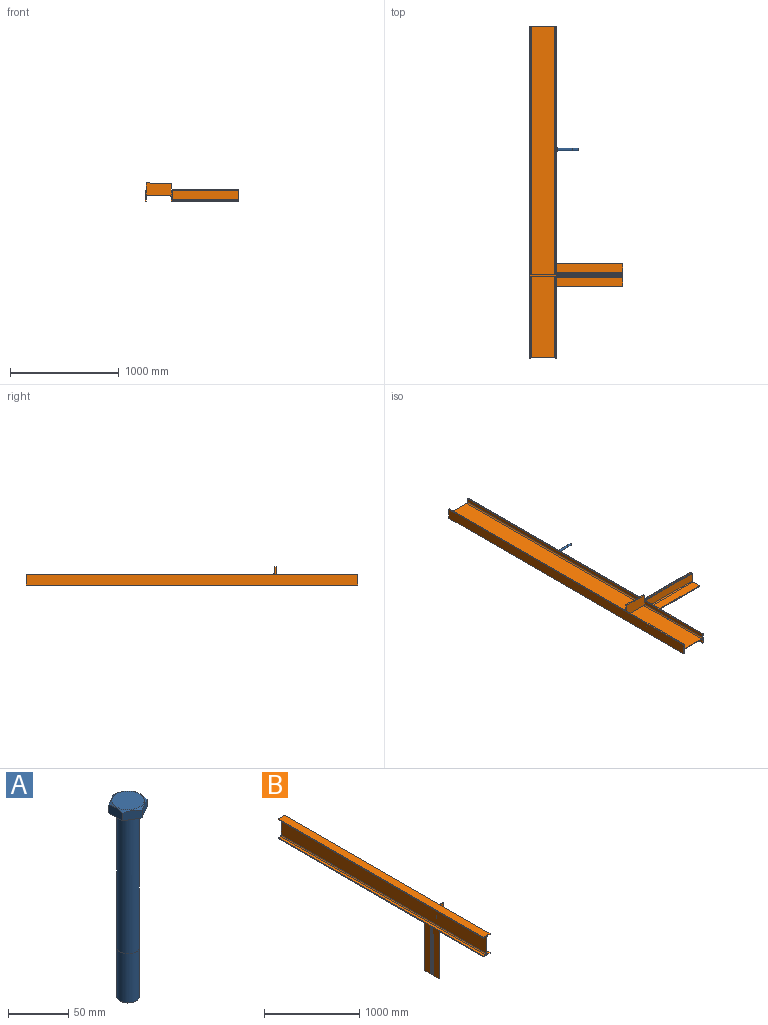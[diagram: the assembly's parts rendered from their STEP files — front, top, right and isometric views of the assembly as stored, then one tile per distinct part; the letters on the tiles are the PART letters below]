
ASSEMBLY  parts=2 mates=1
PART A: 17 faces, bbox 33x33x200.4 mm
  f0: cylinder r=9.53mm len=138.94mm, axis (0,0,-1), area 8315.1mm2, adj f1,f7
  f1: torus R=10.29mm, axis (0,0,1), area 73.7mm2, adj f0,f6
  f2: cylinder r=13.49mm len=26.99mm, axis (0,0,-1), area 32.3mm2, adj f6,f8
  f3: cone r=13.49mm half-angle=60deg, axis (0,0,-1), area 156mm2, adj f9,f10,f11,f12,f13,f14,f15
  f4: cylinder r=9.42mm len=50.04mm, axis (0,0,-1), area 2960.7mm2, adj f5,f7
  f5: cone r=8.66mm half-angle=45deg, axis (0,0,1), area 61.2mm2, adj f4,f16
  f6: plane 26.99x26.99mm, normal (0,0,-1), area 239.6mm2, adj f1,f2
  f7: plane 19.05x19.05mm, normal (0,0,-1), area 6.4mm2, adj f0,f4
  f8: plane 33x28.58mm, normal (0,0,-1), area 135.1mm2, adj f2,f10,f11,f12,f13,f14,f15
  f9: plane 26.99x26.99mm, normal (0,0,1), area 572mm2, adj f3
  f10: plane 16.5x9.08mm, normal (1,0,0), area 142.6mm2, adj f3,f8,f11,f15
  f11: plane 14.29x9.08mm, normal (0.5,-0.87,0), area 142.5mm2, adj f3,f8,f10,f12
  f12: plane 14.29x9.08mm, normal (-0.5,-0.87,0), area 142.6mm2, adj f3,f8,f11,f13
  f13: plane 16.5x9.08mm, normal (-1,0,0), area 142.6mm2, adj f3,f8,f12,f14
  f14: plane 14.29x9.08mm, normal (-0.5,0.87,0), area 142.6mm2, adj f3,f8,f13,f15
  f15: plane 14.29x9.08mm, normal (0.5,0.87,0), area 142.6mm2, adj f3,f8,f10,f14
  f16: plane 17.31x17.31mm, normal (0,0,-1), area 235.3mm2, adj f5
PART B: 50 faces, bbox 166.2x3048x860.3 mm
  f0: plane 2286x36mm, normal (0,0,1), area 82306.3mm2, adj f13,f15,f24,f49
  f1: plane 2286x212.6mm, normal (1,0,0), area 485999mm2, adj f15,f17,f24,f49
  f2: plane 2286x36mm, normal (0,0,-1), area 82306.3mm2, adj f17,f19,f24,f49
  f3: cylinder r=12.16mm len=749.3mm, axis (0,1,0), area 12323.9mm2, adj f14,f16,f23,f48
  f4: cylinder r=12.16mm len=749.3mm, axis (0,1,0), area 12323.9mm2, adj f16,f18,f23,f48
  f5: plane 100.58x12.7mm, normal (0,0,-1), area 1277.4mm2, adj f11,f13,f33,f43
  f6: plane 2274.15x100.58mm, normal (0,0,-1), area 228036mm2, adj f11,f13,f24,f37,f38,f39,f40,f41
  f7: cylinder r=12.16mm len=3048mm, axis (0,1,0), area 50131mm2, adj f8,f22,f23,f24
  f8: plane 3048x212.6mm, normal (-1,0,0), area 647998.7mm2, adj f7,f9,f23,f24
  f9: cylinder r=12.16mm len=3048mm, axis (0,1,0), area 50131mm2, adj f8,f10,f23,f24
  f10: plane 3048x36mm, normal (0,0,1), area 109741.7mm2, adj f9,f11,f23,f24
  f11: plane 3048x619.13mm, normal (-1,0,0), area 152902.9mm2, adj f5,f6,f10,f12,f23,f24,f26,f32
  f12: plane 750.15x100.58mm, normal (0,0,-1), area 74746mm2, adj f11,f13,f23,f27,f28,f29,f30,f31
  f13: plane 3048x9.53mm, normal (1,0,0), area 29032.2mm2, adj f0,f5,f6,f12,f14,f23,f24,f25
  f14: plane 749.3x36mm, normal (0,0,1), area 26978.2mm2, adj f3,f13,f23,f48
  f15: cylinder r=12.16mm len=2286mm, axis (0,1,0), area 37598.2mm2, adj f0,f1,f24,f49
  f16: plane 749.3x212.6mm, normal (1,0,0), area 159299.7mm2, adj f3,f4,f23,f48
  f17: cylinder r=12.16mm len=2286mm, axis (0,1,0), area 37598.2mm2, adj f1,f2,f24,f49
  f18: plane 749.3x36mm, normal (0,0,-1), area 26978.2mm2, adj f4,f19,f23,f48
  f19: plane 3048x9.53mm, normal (1,0,0), area 29032.2mm2, adj f2,f18,f20,f23,f24,f45
  f20: plane 3048x100.58mm, normal (0,0,1), area 306580mm2, adj f19,f21,f23,f24
  f21: plane 3048x9.53mm, normal (-1,0,0), area 29032.2mm2, adj f20,f22,f23,f24
  f22: plane 3048x36mm, normal (0,0,-1), area 109741.7mm2, adj f7,f21,f23,f24
  f23: plane 250.7x100.58mm, normal (0,-1,0), area 3149mm2, adj f3,f4,f7,f8,f9,f10,f11,f12
  f24: plane 250.7x100.58mm, normal (0,1,0), area 3149mm2, adj f0,f1,f2,f6,f7,f8,f9,f10
  f25: plane 5.5x1.02mm, normal (0,0,1), area 4.9mm2, adj f13,f27,f33,f34
  f26: plane 101.6x101.6mm, normal (0,0,-1), area 1265.1mm2, adj f11,f27,f28,f29,f30,f31,f32,f33
  f27: cylinder r=3.17mm len=609.6mm, axis (0,0,-1), area 3040.3mm2, adj f12,f25,f26,f28,f34
  f28: plane 609.6x82.55mm, normal (0,-1,0), area 50322.5mm2, adj f12,f26,f27,f29
  f29: cylinder r=9.52mm len=609.6mm, axis (0,0,-1), area 9120.8mm2, adj f12,f26,f28,f30
  f30: plane 609.6x82.55mm, normal (1,0,0), area 50322.5mm2, adj f12,f26,f29,f31
  f31: cylinder r=3.17mm len=609.6mm, axis (0,0,-1), area 3040.3mm2, adj f12,f26,f30,f32
  f32: plane 609.6x3.18mm, normal (0,-1,0), area 1935.5mm2, adj f11,f12,f26,f31
  f33: plane 609.6x101.6mm, normal (0,1,0), area 61935.4mm2, adj f5,f11,f25,f26,f34
  f34: plane 609.6x3.18mm, normal (1,0,0), area 1935.5mm2, adj f25,f26,f27,f33
  f35: plane 5.5x1.02mm, normal (0,0,1), area 4.9mm2, adj f13,f37,f43,f44
  f36: plane 101.6x101.6mm, normal (0,0,-1), area 1265.1mm2, adj f11,f37,f38,f39,f40,f41,f42,f43
  f37: cylinder r=3.17mm len=609.6mm, axis (0,0,-1), area 3040.3mm2, adj f6,f35,f36,f38,f44
  f38: plane 609.6x82.55mm, normal (0,1,0), area 50322.5mm2, adj f6,f36,f37,f39
  f39: cylinder r=9.52mm len=609.6mm, axis (0,0,-1), area 9120.8mm2, adj f6,f36,f38,f40
  f40: plane 609.6x82.55mm, normal (1,0,0), area 50322.5mm2, adj f6,f36,f39,f41
  f41: cylinder r=3.17mm len=609.6mm, axis (0,0,-1), area 3040.3mm2, adj f6,f36,f40,f42
  f42: plane 609.6x3.18mm, normal (0,1,0), area 1935.5mm2, adj f6,f11,f36,f41
  f43: plane 609.6x101.6mm, normal (0,-1,0), area 61935.4mm2, adj f5,f11,f35,f36,f44
  f44: plane 609.6x3.18mm, normal (1,0,0), area 1935.5mm2, adj f35,f36,f37,f43
  f45: plane 65.6x12.7mm, normal (0,0,1), area 833.1mm2, adj f19,f47,f48,f49
  f46: plane 62.65x12.7mm, normal (0,0,-1), area 795.6mm2, adj f13,f47,f48,f49
  f47: plane 231.65x12.7mm, normal (1,0,-0.01), area 2942.2mm2, adj f45,f46,f48,f49
  f48: plane 231.65x113.47mm, normal (0,-1,0), area 25887.1mm2, adj f3,f4,f14,f16,f18,f45,f46,f47
  f49: plane 231.65x113.47mm, normal (0,1,0), area 25887.1mm2, adj f0,f1,f2,f15,f17,f45,f46,f47
PLACE A rot(axis=(0.71,0,-0.71),180deg) t=(135.27,263.32,125.48)mm
PLACE B rot(axis=(0,-1,0),90deg) t=(125.35,-127,125.35)mm
MATE fastened A.f2 <-> B.f6  axis (-1,0,0) through (125.35,263.32,125.48)mm
